# Revit family: BETSY1
name_source: partatom
category: Furniture
units: mm (PartAtom-declared; Revit-internal decimal feet)

## family parameters
Always vertical = Yes
Cut with Voids When Loaded = No
OmniClass Number = 23.40.00.00
OmniClass Title = Equipment and Furnishings
Room Calculation Point = No
Shared = No
Work Plane-Based = No

## types (6) — shared parameters
Assembly Code = E2020200
Back = Gresham - Camira Synergy Merge
Black Plastic = Gresham - Black Plastic
Manufacturer = Gresham Office Funiture
Metal Frame = Gresham - Chrome
Model = BETSY
Range = SEATING
Seat = Gresham - Camira Synergy Merge
URL = www.gof.co.uk
Wooden Legs = Gresham - DARK WALNUT

## per-type parameters (varying)
| type | Four Star Base (Castors) | Four Star Base (Glides) | Pyramid Base (Castors) | Pyramid Base (Glides) | Skid Frame | Wooden Frame |
| BETZ | No | No | No | No | No | Yes |
| BETS | No | No | No | No | Yes | No |
| BET4 | No | Yes | No | No | No | No |
| BET4W | Yes | No | No | No | No | No |
| BETP | No | No | No | Yes | No | No |
| BETPW | No | No | Yes | No | No | No |

note: column(s) folded — value = type name in every type: Product Code

## geometry (parser evidence)
native form markers: Sweep x13
no freeform markers — native parametric forms only
